# Revit family: 280550xc (200)
name_source: partatom
category: Generic Models
units: mm (PartAtom-declared; Revit-internal decimal feet)

## family parameters
Always vertical = Yes
Can host rebar = No
Cut with Voids When Loaded = No
Part Type = Normal
Room Calculation Point = No
Round Connector Dimension = Use Diameter
Shared = Yes
Work Plane-Based = No

## types (1)
- 280550XC
    4.010.00.12 Stand des Herstellerkatalogs = 20180713
    4.010.00.13 Sprache der Datei = DEU
    4.010.00.14 Kennungen der Projektländer, für die die Datei gültig ist = DE
    4.010.00.2 Sheet number of the guideline = 4
    4.010.00.3 Date of issuance (month) of guideline = 201805
    4.010.00.4 Manufacturer name = KESSEL AG
    4.010.00.7 Comment = www.kessel.de
    4.010.00.8 Producer ID number = 4026092000007
    4.100.00.4 Product indentification = Entwässerung
    4.100.00.5 Main groups of wares = Hebeanlage
    4.110.00.4 Product indentification = Hebeanlage Aqualift S Compact
    4.110.00.6 Product classification = Hebeanlage
    4.200.00.3 Variant / Variant type / Accessories-name = 6
    4.250.00.3 Variant / Variant type / Accessories-name = vertikal
    4.260.00.3 Variant / Variant type / Accessories-name = Trockenläuferpumpe
    4.300.00.3 Variant / Variant type / Accessories-name = einstufig
    4.350.00.3 Variant / Variant type / Accessories-name = normalansaugend
    4.400.00.3 Variant / Variant type / Accessories-name = E-Motor für Wechselstrom
    4.460.00.3 Variant / Variant type / Accessories-name = direkt
    4.500.00.3 Variant / Variant type / Accessories-name = Kunststoff, Edelstahl
    4.700.00.10 Phase = 0
    4.700.00.11 Stern-/Dreieck-Anlaufschaltung bei Dreiphasenanschluss oder Drehstrom = 50 Hz
    4.700.00.12 Frequency = 0
    4.700.00.13 Type of protection = F
    4.700.00.15 Increased safety class = 35 °C
    4.700.00.16 Maximum temperature of pumped medium = 0 °C
    4.700.00.22 Maximum shaft output (P2) per pump/drive = 0 W
    4.700.00.23 Nominal speed of motor = 46.666667
    4.700.00.24 Nominal speed / maximum speed n = 46.666667
    4.700.00.25 Minimum speed at internal speed adjustment = 0
    4.700.00.26 Maximum power consumption per pump / drive = 2.5
    4.700.00.27 Starting current = 6.9
    4.700.00.28 Motor pump shaft = durchgehend
    4.700.00.4 Product indentification = Hebeanlage Aqualift S Compact, Tronic, GTF500, resist., Bodenpl., befl.
    4.700.00.6 Type of connection = 32
    4.700.00.7 Nominal connection size on pressure side = 100
    4.700.00.8 Nominal connection size on suction side = 100
    4.700.00.9 Voltage = 0
    4.710.01.4 Designation of closed-loop control = 20
    4.710.01.5 Load regulation = 0
    4.710.01.6 Option to connect to building automation = 10
    4.710.02.3 Free passage = 10 mm  [stored 0.0328084 ft]
    4.710.02.4 Attached pump control = 1
    4.710.02.5 Cutting device = 0
    4.710.02.6 Duty type = S1
    4.710.02.8 Area of application of wastewater pump = 2
    4.710.03.3 Type of dimensions = 2
    4.710.03.4 Length = 620 mm  [stored 2.03412 ft]
    4.710.03.5 Width = 580 mm  [stored 1.90289 ft]
    4.710.03.6 Height = 490 mm  [stored 1.60761 ft]
    4.710.03.7 Mass (net) = 16.85 kg
    4.810.00.3 Producer order number = 280550XC
    4.810.00.4 DATANORM number = 280550XC
    4.810.00.6 GTIN number = 04026092082652
    4.810.00.7 Media- connection number = 197
    4.810.00.9 Order quantity (multiplicator) = 1
    ARTICLENO = NB
    BOMINFO = LINA
    CATALOG = KESSEL
    Default Elevation = 0 mm  [stored 0 ft]
    LINA = 280550XC
    LINK = https://www.kessel.de
    Manufacturer = KESSEL
    Model = 280550XC
    NB = 280550XC (200)
    NBSYN = $SA810ID03. ($LODLEVEL.)
    NN = Lifting station Aqualift S compact
    PRC_SPECIFICATIONLINK = https://ausschreiben.de
    PROCUREDATALASTUPDATE = 2024-05-22T12:17:24.487394111+01:00
    PROCURELINK = p.caden.as/kessel/280550XC
    PROCUREWEBLINK = https://p.caden.as
    SA700ID08 = 230 V
    SA700ID10 = No
    SA700ID21 = 800
    SA700ID29 = RWDR
    SA700ID30 = 1
    SA700ID31 = 1
    SA700ID32 = 16.85 kg
    SA700ID33 = 1 W
    SA700ID34 = 12
    SA700ID37 = 8000 mm
    SA700ID46 = yes
    SA700ID47 = no
    SA700ID48 = no
    SA700ID49 = Protection Class I
    SA700ID50 = internal
    SUPPLIER = KESSEL

note: [stored X ft] marks values corroborated as IEEE doubles in the binary element streams (Revit-internal decimal feet)

## geometry (parser evidence)
native form markers: Sweep x12
no freeform markers — native parametric forms only
